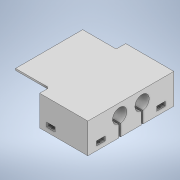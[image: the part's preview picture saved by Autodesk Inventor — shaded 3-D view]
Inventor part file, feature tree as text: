
AUTODESK INVENTOR PART (.ipt)
format: ipt  version: 2020 (Build 240168000, 168)  size: 237,056 bytes
history: native  units: mm
features: extrude x5, sketch x3, plane x1, chamfer x1
ambient origin geometry x8: Origin, YZ Plane, XZ Plane, XY Plane, X Axis, Y Axis, Z Axis, Center Point
bodies: Solid1 (feature_tree)
feature tree (10):
  sketch  "Sketch1"  dims[d0=5.0mm d3=100.0mm]
  extrude  "Extrusion1"  Depth=100.0mm
  extrude  "Extrusion2"  Depth=5.0mm
  extrude  "Extrusion4"  Depth=5.0mm
  sketch  "Sketch3"  dims[d4=95.0mm d5=5.0mm]
  extrude  "Extrusion6"  Depth=2.0mm TaperAngle=0.0deg
  plane  "Work Plane1"
  extrude  "Extrusion7"  Depth=33.0mm TaperAngle=0.0deg
  chamfer  "Chamfer1"  Distance=16.6mm
  sketch  "Sketch5"  dims[d6=5.0mm d7=5.0mm d8=2.0mm d9=0.0mm d10=33.0mm d11=0.0mm d14=16.6mm d15=16.6mm d16=26.0mm d17=22.0mm d18=37.0mm d19=10.0mm d20=0.0mm d21=20.0mm d22=20.0mm d24=12.0mm d25=8.0mm d28=12.0mm d29=0.0mm d34=-5.0mm d35=5.0mm d36=0.0mm d37=2.0mm d38=20.0mm d39=20.0mm d40=2.0mm d41=2.0mm d42=45.0deg d43=0.872665mm]
